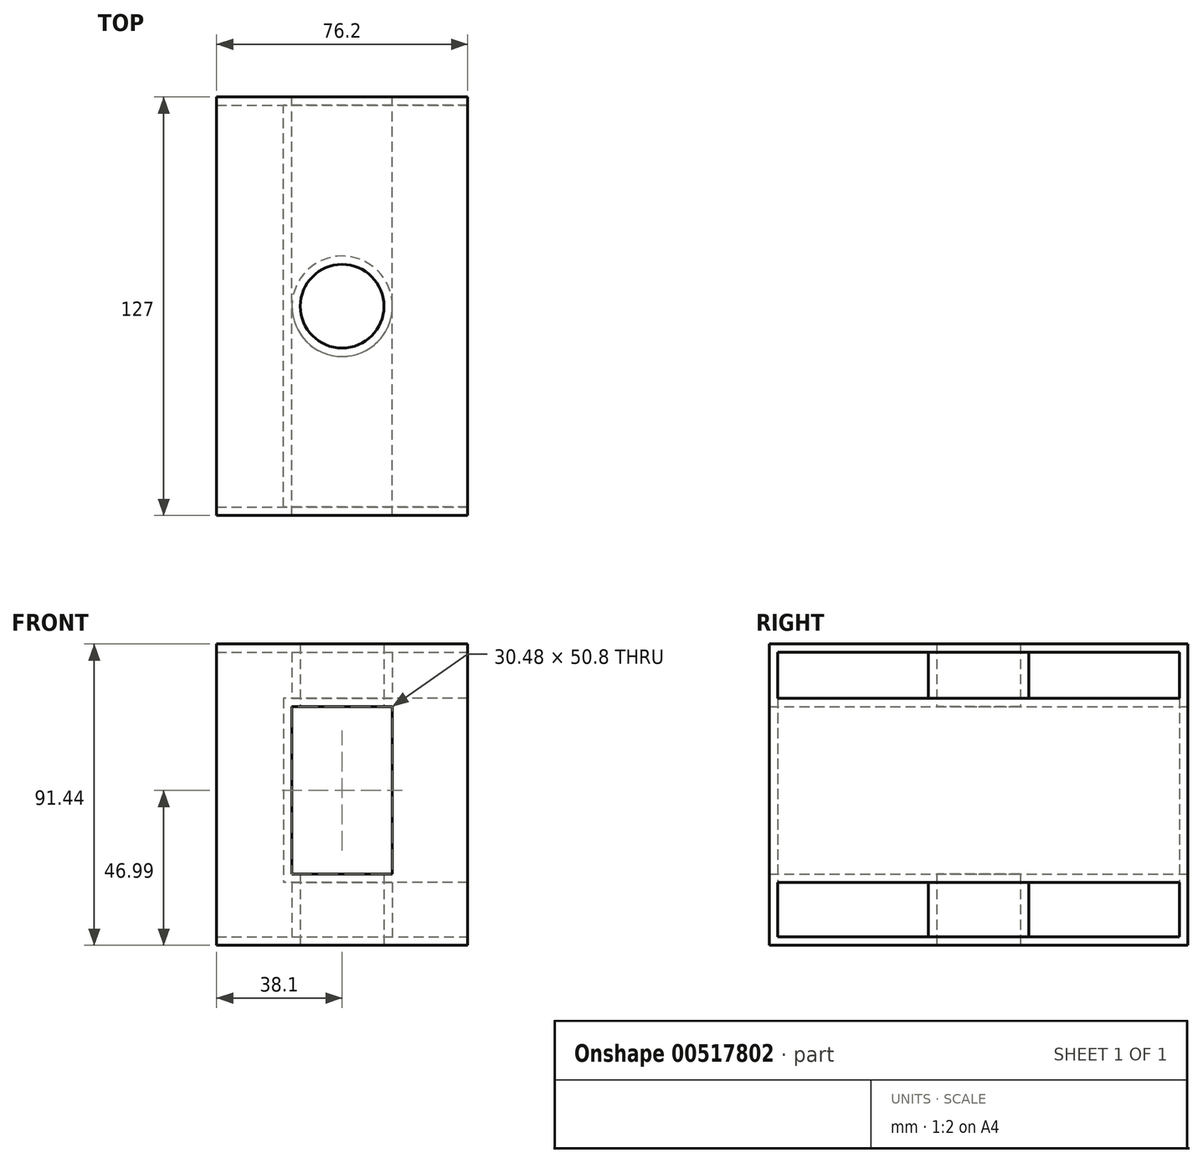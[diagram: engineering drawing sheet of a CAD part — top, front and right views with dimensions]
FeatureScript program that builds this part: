
annotation { "Feature Type Name" : "Feature", "Feature Type Description" : "" }
export const myFeature = defineFeature(function(context is Context, id is Id, definition is map)
    precondition{}
    {
        {
            var Q0;
            Q0=qCreatedBy(makeId("Top.planeOp"),FACE);
            var sketch = newSketch(context, id + "F0", { "sketchPlane" : qUnion([Q0])});
            skLineSegment(sketch, "E0.bottom", {"start": v(-54.22, 127) * mm, "end": v(21.98, 127) * mm});
            skLineSegment(sketch, "E0.top", {"start": v(-54.22, 0) * mm, "end": v(21.98, 0) * mm});
            skLineSegment(sketch, "E0.left", {"start": v(-54.22, 127) * mm, "end": v(-54.22, 0) * mm});
            skLineSegment(sketch, "E0.right", {"start": v(21.98, 127) * mm, "end": v(21.98, 0) * mm});
            skCircle(sketch, "E1", {"center": v(-16.12, 63.5) * mm, "radius": 12.7 * mm});
            skSolve(sketch);
        }
        {
            var Q0;
            Q0 = qSketchRegion(id + "F0", true);
            extrude(context, id + "F1", {"entities" : qUnion([Q0]), "depth" : 91.44 * mm, "offsetDistance" : 25.4 * mm});
        }
        {
            var Q0;
            Q0=makeQuery(id+"F1.opExtrude","SWEPT_FACE",FACE,{"disambiguationData":[OSD([sQuery(id+"F0.wireOp",EDGE,"E0.bottom")])]});
            var sketch = newSketch(context, id + "F2", { "sketchPlane" : qUnion([Q0])});
            skLineSegment(sketch, "E2.bottom", {"start": v(0.88, 72.4) * mm, "end": v(31.36, 72.4) * mm});
            skLineSegment(sketch, "E2.top", {"start": v(0.88, 21.6) * mm, "end": v(31.36, 21.6) * mm});
            skLineSegment(sketch, "E2.left", {"start": v(0.88, 72.4) * mm, "end": v(0.88, 21.6) * mm});
            skLineSegment(sketch, "E2.right", {"start": v(31.36, 72.4) * mm, "end": v(31.36, 21.6) * mm});
            skSolve(sketch);
        }
        {
            var Q0;
            Q0 = qSketchRegion(id + "F2", true);
            extrude(context, id + "F3", {"entities" : qUnion([Q0]), "operationType" : NewBodyOperationType.REMOVE, "oppositeDirection" : true, "depth" : 143.26 * mm, "offsetDistance" : 25.4 * mm});
        }
        {
            var Q0;
            Q0=makeQuery(id+"F1.opExtrude","SWEPT_FACE",FACE,{"disambiguationData":[OSD([sQuery(id+"F0.wireOp",EDGE,"E0.right")])]});
            var Q1;
            Q1=makeQuery(id+"F1.opExtrude","SWEPT_FACE",FACE,{"disambiguationData":[OSD([sQuery(id+"F0.wireOp",EDGE,"E0.left")])]});
            shell(context, id + "F4", {"entities" : qUnion([Q0, Q1]), "thickness" : 2.54 * mm});
        }
        {
            var Q0;
            Q0=makeQuery(id+"F4.opShell","OFFSET_FACE",FACE,{"disambiguationData":[OSD([sQuery(id+"F2.wireOp",EDGE,"E2.left")])]});
            extrude(context, id + "F5", {"entities" : qUnion([Q0]), "operationType" : NewBodyOperationType.ADD, "depth" : 20.32 * mm, "offsetDistance" : 25.4 * mm});
        }
    });
